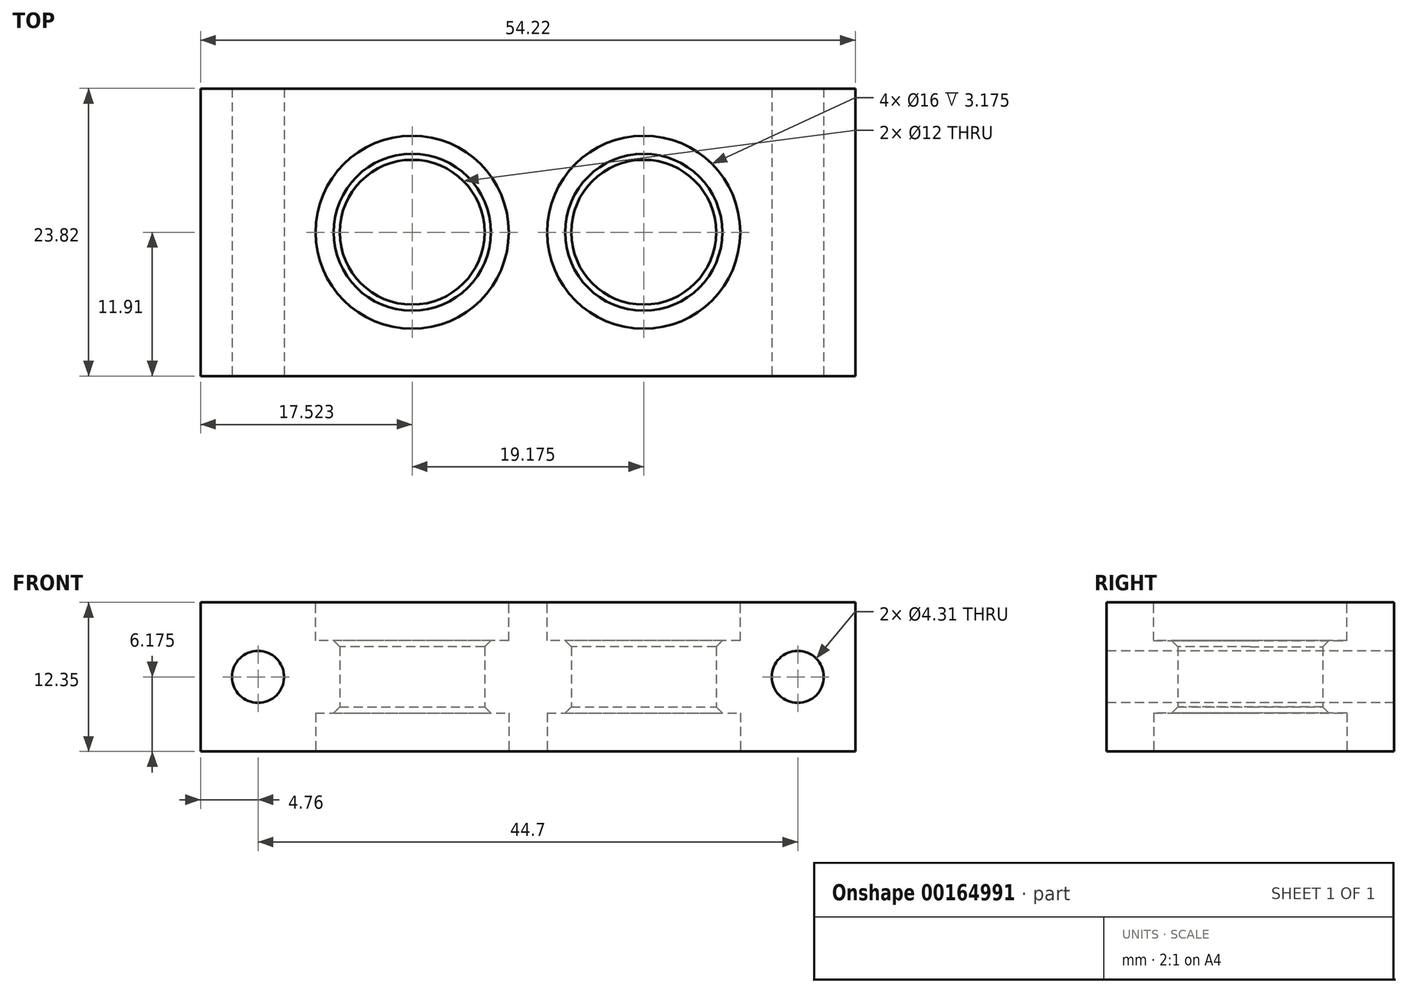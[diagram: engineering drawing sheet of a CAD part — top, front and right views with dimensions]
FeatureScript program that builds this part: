
annotation { "Feature Type Name" : "Feature", "Feature Type Description" : "" }
export const myFeature = defineFeature(function(context is Context, id is Id, definition is map)
    precondition{}
    {
        {
            var Q0;
            Q0=qCreatedBy(makeId("Top.planeOp"),FACE);
            var sketch = newSketch(context, id + "F0", { "sketchPlane" : qUnion([Q0])});
            skLineSegment(sketch, "E0.bottom", {"start": v(27.11, -11.9) * mm, "end": v(-27.11, -11.9) * mm});
            skLineSegment(sketch, "E0.top", {"start": v(27.11, 11.9) * mm, "end": v(-27.11, 11.9) * mm});
            skLineSegment(sketch, "E0.left", {"start": v(27.11, -11.9) * mm, "end": v(27.11, 11.9) * mm});
            skLineSegment(sketch, "E0.right", {"start": v(-27.11, -11.9) * mm, "end": v(-27.11, 11.9) * mm});
            skPoint(sketch, "E0.middle", {"position": v(0, 0) * mm});
            skCircle(sketch, "E1", {"center": v(9.59, 0) * mm, "radius": 6 * mm});
            skCircle(sketch, "E2", {"center": v(9.59, 0) * mm, "radius": 8 * mm, "construction": true});
            skCircle(sketch, "E3", {"center": v(-9.59, 0) * mm, "radius": 6 * mm});
            skLineSegment(sketch, "E4", {"start": v(-9.59, 0) * mm, "end": v(9.59, 0) * mm, "construction": true});
            skCircle(sketch, "E5", {"center": v(-9.59, 0) * mm, "radius": 8 * mm, "construction": true});
            skSolve(sketch);
        }
        {
            var Q0;
            Q0 = qSketchRegion(id + "F0", true);
            extrude(context, id + "F1", {"entities" : qUnion([Q0]), "depth" : 12.35 * mm});
        }
        {
            var Q0;
            Q0=makeQuery(id+"F1.opExtrude","CAP_FACE",FACE,{"disambiguationData":[OSD([sQuery(id+"F0.wireOp",EDGE,"E0.bottom"),sQuery(id+"F0.wireOp",EDGE,"E0.top"),sQuery(id+"F0.wireOp",EDGE,"E0.left"),sQuery(id+"F0.wireOp",EDGE,"E0.right"),sQuery(id+"F0.wireOp",EDGE,"E1")])],"isStart":false});
            var sketch = newSketch(context, id + "F2", { "sketchPlane" : qUnion([Q0])});
            skCircle(sketch, "E6", {"center": v(9.59, 0) * mm, "radius": 8 * mm});
            skCircle(sketch, "E7", {"center": v(-9.59, 0) * mm, "radius": 8 * mm});
            skSolve(sketch);
        }
        {
            var Q0;
            Q0 = qSketchRegion(id + "F2", true);
            extrude(context, id + "F3", {"entities" : qUnion([Q0]), "operationType" : NewBodyOperationType.REMOVE, "oppositeDirection" : true, "depth" : 3.17 * mm});
        }
        {
            var Q0;
            Q0=makeQuery(id+"F1.opExtrude","CAP_FACE",FACE,{"disambiguationData":[OSD([sQuery(id+"F0.wireOp",EDGE,"E0.bottom"),sQuery(id+"F0.wireOp",EDGE,"E0.top"),sQuery(id+"F0.wireOp",EDGE,"E0.left"),sQuery(id+"F0.wireOp",EDGE,"E0.right"),sQuery(id+"F0.wireOp",EDGE,"E1")])],"isStart":true});
            var sketch = newSketch(context, id + "F4", { "sketchPlane" : qUnion([Q0])});
            skCircle(sketch, "E8", {"center": v(9.59, 0) * mm, "radius": 8 * mm});
            skCircle(sketch, "E9", {"center": v(-9.59, 0) * mm, "radius": 8 * mm});
            skSolve(sketch);
        }
        {
            var Q0;
            Q0 = qSketchRegion(id + "F4", true);
            extrude(context, id + "F5", {"entities" : qUnion([Q0]), "operationType" : NewBodyOperationType.REMOVE, "oppositeDirection" : true, "depth" : 3.17 * mm});
        }
        {
            var Q0;
            Q0=makeQuery(id+"F1.opExtrude","SWEPT_FACE",FACE,{"disambiguationData":[OSD([sQuery(id+"F0.wireOp",EDGE,"E0.bottom")])]});
            var sketch = newSketch(context, id + "F6", { "sketchPlane" : qUnion([Q0])});
            skLineSegment(sketch, "E10.bottom", {"start": v(-27.11, 6.17) * mm, "end": v(-22.35, 6.17) * mm, "construction": true});
            skLineSegment(sketch, "E10.top", {"start": v(-27.11, 0) * mm, "end": v(-22.35, 0) * mm, "construction": true});
            skLineSegment(sketch, "E10.left", {"start": v(-27.11, 6.17) * mm, "end": v(-27.11, 0) * mm, "construction": true});
            skLineSegment(sketch, "E10.right", {"start": v(-22.35, 6.17) * mm, "end": v(-22.35, 0) * mm, "construction": true});
            skLineSegment(sketch, "E11.bottom", {"start": v(27.11, 6.17) * mm, "end": v(22.35, 6.17) * mm, "construction": true});
            skLineSegment(sketch, "E11.top", {"start": v(27.11, 0) * mm, "end": v(22.35, 0) * mm, "construction": true});
            skLineSegment(sketch, "E11.left", {"start": v(27.11, 6.17) * mm, "end": v(27.11, 0) * mm, "construction": true});
            skLineSegment(sketch, "E11.right", {"start": v(22.35, 6.17) * mm, "end": v(22.35, 0) * mm, "construction": true});
            skCircle(sketch, "E12", {"center": v(-22.35, 6.17) * mm, "radius": 2.15 * mm});
            skCircle(sketch, "E13", {"center": v(22.35, 6.17) * mm, "radius": 2.15 * mm});
            skSolve(sketch);
        }
        {
            var Q0;
            Q0 = qSketchRegion(id + "F6", true);
            var Q1;
            Q1=makeQuery(id+"F1.opExtrude","SWEPT_FACE",FACE,{"disambiguationData":[OSD([sQuery(id+"F0.wireOp",EDGE,"E0.top")])]});
            extrude(context, id + "F7", {"entities" : qUnion([Q0]), "operationType" : NewBodyOperationType.REMOVE, "endBound" : BoundingType.UP_TO_SURFACE, "oppositeDirection" : true, "endBoundEntityFace" : qUnion([Q1]), "depth" : 25.4 * mm});
        }
        {
            var Q0;
            Q0=makeQuery(id+"F3.boolean.opBoolean","COPY",EDGE,{"derivedFrom":makeQuery(id+"F3.opExtrude","CAP_EDGE",EDGE,{"disambiguationData":[OSD([sQuery(id+"F2.wireOp",EDGE,"E6")])],"isStart":true})});
            var Q1;
            Q1=makeQuery(id+"F3.boolean.opBoolean","INTERSECT",EDGE,{"derivedFrom":[makeQuery(id+"F1.opExtrude","SWEPT_FACE",FACE,{"disambiguationData":[OSD([sQuery(id+"F0.wireOp",EDGE,"E1")])]}),makeQuery(id+"F3.opExtrude","CAP_FACE",FACE,{"disambiguationData":[OSD([sQuery(id+"F2.wireOp",EDGE,"E6")])],"isStart":false})]});
            var Q2;
            Q2=makeQuery(id+"F5.boolean.opBoolean","INTERSECT",EDGE,{"derivedFrom":[makeQuery(id+"F1.opExtrude","SWEPT_FACE",FACE,{"disambiguationData":[OSD([sQuery(id+"F0.wireOp",EDGE,"E1")])]}),makeQuery(id+"F5.opExtrude","CAP_FACE",FACE,{"disambiguationData":[OSD([sQuery(id+"F4.wireOp",EDGE,"E8")])],"isStart":false})]});
            var Q3;
            Q3=makeQuery(id+"F5.boolean.opBoolean","COPY",EDGE,{"derivedFrom":makeQuery(id+"F5.opExtrude","CAP_EDGE",EDGE,{"disambiguationData":[OSD([sQuery(id+"F4.wireOp",EDGE,"E8")])],"isStart":true})});
            var Q4;
            Q4=makeQuery(id+"F5.boolean.opBoolean","COPY",EDGE,{"derivedFrom":makeQuery(id+"F5.opExtrude","CAP_EDGE",EDGE,{"disambiguationData":[OSD([sQuery(id+"F4.wireOp",EDGE,"E9")])],"isStart":true})});
            var Q5;
            Q5=makeQuery(id+"F3.boolean.opBoolean","COPY",EDGE,{"derivedFrom":makeQuery(id+"F3.opExtrude","CAP_EDGE",EDGE,{"disambiguationData":[OSD([sQuery(id+"F2.wireOp",EDGE,"E7")])],"isStart":true})});
            var Q6;
            Q6=makeQuery(id+"F3.boolean.opBoolean","INTERSECT",EDGE,{"derivedFrom":[makeQuery(id+"F1.opExtrude","SWEPT_FACE",FACE,{"disambiguationData":[OSD([sQuery(id+"F0.wireOp",EDGE,"E3")])]}),makeQuery(id+"F3.opExtrude","CAP_FACE",FACE,{"disambiguationData":[OSD([sQuery(id+"F2.wireOp",EDGE,"E7")])],"isStart":false})]});
            var Q7;
            Q7=makeQuery(id+"F5.boolean.opBoolean","INTERSECT",EDGE,{"derivedFrom":[makeQuery(id+"F1.opExtrude","SWEPT_FACE",FACE,{"disambiguationData":[OSD([sQuery(id+"F0.wireOp",EDGE,"E3")])]}),makeQuery(id+"F5.opExtrude","CAP_FACE",FACE,{"disambiguationData":[OSD([sQuery(id+"F4.wireOp",EDGE,"E9")])],"isStart":false})]});
            chamfer(context, id + "F8", {"entities" : qUnion([Q0, Q1, Q2, Q3, Q4, Q5, Q6, Q7]), "width" : 0.5 * mm, "tangentPropagation" : true});
        }
    });
